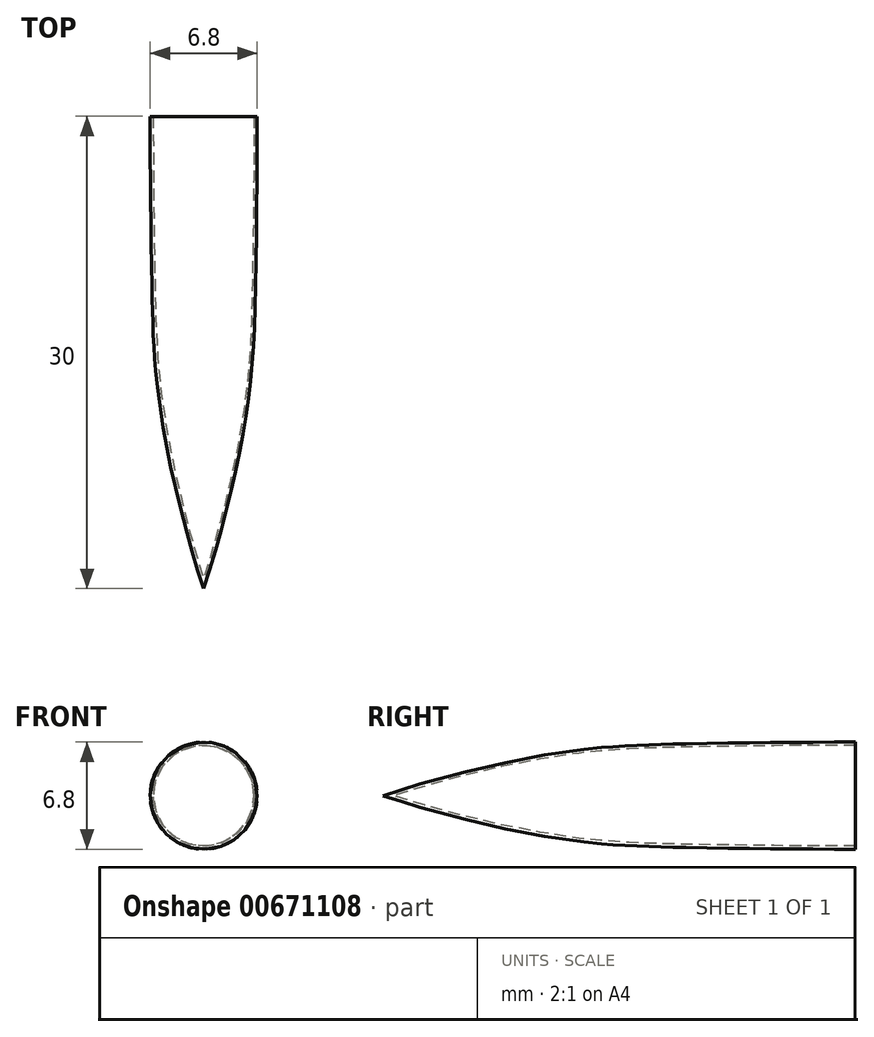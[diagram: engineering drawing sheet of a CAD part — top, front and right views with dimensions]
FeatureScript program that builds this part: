
annotation { "Feature Type Name" : "Feature", "Feature Type Description" : "" }
export const myFeature = defineFeature(function(context is Context, id is Id, definition is map)
    precondition{}
    {
        {
            var Q0;
            Q0=qCreatedBy(makeId("Top.planeOp"),FACE);
            var sketch = newSketch(context, id + "F0", { "sketchPlane" : qUnion([Q0])});
            skLineSegment(sketch, "E0", {"start": v(-42.57, 52.27) * mm, "end": v(-42.57, 22.27) * mm});
            skFitSpline(sketch, "E1", {"points": [v(-39.17, 52.27) * mm, v(-39.27, 41.88) * mm, v(-39.6, 35.3) * mm, v(-40.63, 29.28) * mm, v(-42.57, 22.27) * mm], "startDerivative": vector(0.07, -22.4) * mm, "endDerivative": vector(-8.86, -26.67) * mm});
            skLineSegment(sketch, "E2", {"start": v(-39.17, 52.27) * mm, "end": v(-42.57, 52.27) * mm});
            skSolve(sketch);
        }
        {
            var Q0;
            Q0=qSketchRegion(id+"F0",true);
            var Q1;
            Q1=sQuery(id+"F0.wireOp",EDGE,"E0");
            revolve(context, id + "F1", {"entities" : qUnion([Q0]), "axis" : qUnion([Q1]), "revolveType" : RevolveType.FULL});
        }
        {
            var Q0;
            Q0=makeQuery(id+"F1.opRevolve","SWEPT_FACE",FACE,{"disambiguationData":[OSD([sQuery(id+"F0.wireOp",EDGE,"E2")])]});
            shell(context, id + "F2", {"entities" : qUnion([Q0]), "thickness" : 0.2 * mm});
        }
    });
